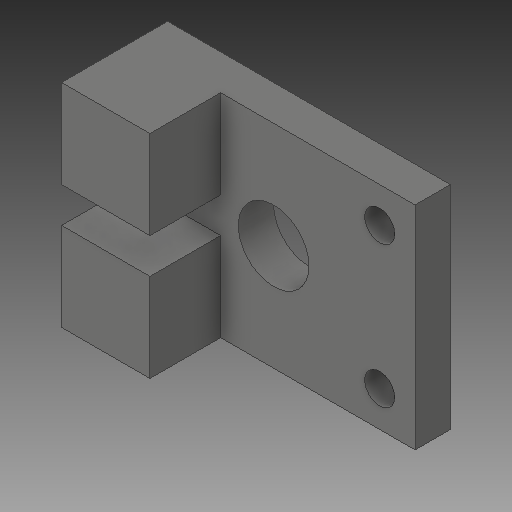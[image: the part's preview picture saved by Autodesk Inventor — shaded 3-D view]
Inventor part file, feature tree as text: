
AUTODESK INVENTOR PART (.ipt)
format: ipt  version: 2019 (Build 230136000, 136)  size: 276,480 bytes
history: native  units: mm
features: reference x4, other x3, extrude x2, sketch x2
ambient origin geometry x8: Origin, YZ Plane, XZ Plane, XY Plane, X Axis, Y Axis, Z Axis, Center Point
bodies: Solid1 (feature_tree)
feature tree (11):
  extrude  "Extrusion1"  Depth=30.0mm
  extrude  "Extrusion2"  Depth=10.0mm
  sketch  "Sketch1"  dims[d4=40.0mm d5=30.0mm]
  reference  "Reference1"
  reference  "Reference2"
  reference  "Reference3"
  reference  "Reference4"
  sketch  "Sketch3"  dims[d6=5.0mm d7=0.0mm d8=10.0mm d9=5.0mm d11=10.0mm d12=0.0mm]
  other  "<userpath>\Stuff\Ajedrez2\YCart.iam"
  other  "YCart.iam"
  other  "YCartFloor:1"
